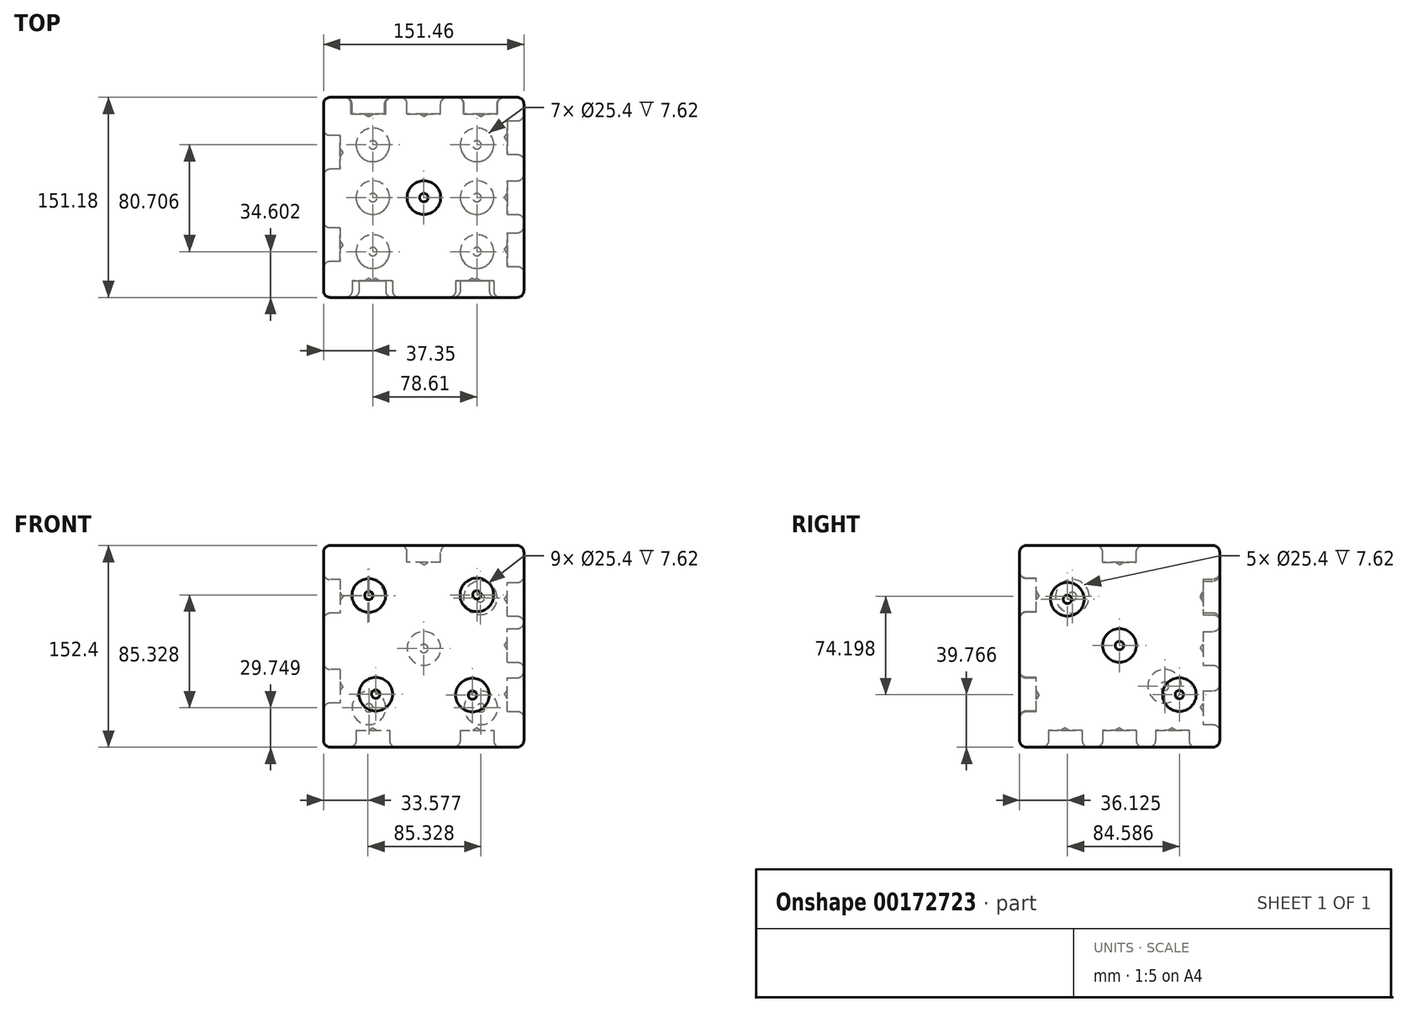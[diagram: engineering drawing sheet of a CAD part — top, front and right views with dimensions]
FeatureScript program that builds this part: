
annotation { "Feature Type Name" : "Feature", "Feature Type Description" : "" }
export const myFeature = defineFeature(function(context is Context, id is Id, definition is map)
    precondition{}
    {
        {
            var Q0;
            Q0=qCreatedBy(makeId("Top.planeOp"),FACE);
            var sketch = newSketch(context, id + "F0", { "sketchPlane" : qUnion([Q0])});
            skLineSegment(sketch, "E0.bottom", {"start": v(-75.87, -75.45) * mm, "end": v(75.59, -75.45) * mm});
            skLineSegment(sketch, "E0.top", {"start": v(-75.87, 75.73) * mm, "end": v(75.59, 75.73) * mm});
            skLineSegment(sketch, "E0.left", {"start": v(-75.87, -75.45) * mm, "end": v(-75.87, 75.73) * mm});
            skLineSegment(sketch, "E0.right", {"start": v(75.59, -75.45) * mm, "end": v(75.59, 75.73) * mm});
            skSolve(sketch);
        }
        {
            var Q0;
            Q0=makeQuery(id+"F0.imprint","IMPRINT",FACE,{"disambiguationData":[TD([[makeQuery(id+"F0.imprint","IMPRINT",EDGE,{"derivedFrom":sQuery(id+"F0.wireOp",EDGE,"E0.bottom")}),1.0]])]});
            extrude(context, id + "F1", {"entities" : qUnion([Q0]), "depth" : 127 * mm});
        }
        {
            var Q0;
            Q0=makeQuery(id+"F1.opExtrude","CAP_FACE",FACE,{"disambiguationData":[OSD([sQuery(id+"F0.wireOp",EDGE,"E0.bottom"),sQuery(id+"F0.wireOp",EDGE,"E0.top"),sQuery(id+"F0.wireOp",EDGE,"E0.left"),sQuery(id+"F0.wireOp",EDGE,"E0.right")])],"isStart":false});
            extrude(context, id + "F2", {"entities" : qUnion([Q0]), "operationType" : NewBodyOperationType.ADD, "depth" : 25.4 * mm});
        }
        {
            var Q0;
            Q0=makeQuery(id+"F2.opExtrude","CAP_FACE",FACE,{"disambiguationData":[OSD([sQuery(id+"F0.wireOp",EDGE,"E0.bottom"),sQuery(id+"F0.wireOp",EDGE,"E0.top"),sQuery(id+"F0.wireOp",EDGE,"E0.left"),sQuery(id+"F0.wireOp",EDGE,"E0.right")])],"isStart":false});
            var sketch = newSketch(context, id + "F3", { "sketchPlane" : qUnion([Q0])});
            skCircle(sketch, "E1", {"center": v(0, 0) * mm, "radius": 13.7 * mm});
            skSolve(sketch);
        }
        {
            var Q0;
            Q0=sQuery(id+"F3.wireOp",VERTEX,"E1.center");
            var Q1;
            Q1=makeQuery(id+"F1.opExtrude","SWEPT_BODY",BODY,{"disambiguationData":[OSD([sQuery(id+"F0.wireOp",EDGE,"E0.bottom"),sQuery(id+"F0.wireOp",EDGE,"E0.top"),sQuery(id+"F0.wireOp",EDGE,"E0.left"),sQuery(id+"F0.wireOp",EDGE,"E0.right")])]});
            hole(context, id + "F4", {"style" : HoleStyle.C_BORE, "endStyle" : HoleEndStyle.BLIND, "holeDiameter" : 6.35 * mm, "cBoreDiameter" : 25.4 * mm, "cBoreDepth" : 12.7 * mm, "holeDepth" : 12.7 * mm, "startFromSketch" : true, "locations" : qUnion([Q0]), "scope" : qUnion([Q1])});
        }
        {
            var Q0;
            Q0=makeQuery(id+"F4.hole-0.boolean.opBoolean","COPY",FACE,{"derivedFrom":makeQuery(id+"F4.hole-0.opRevolve","SWEPT_FACE",FACE,{"disambiguationData":[OSD([sQuery(id+"F4.hole-0.sketch.wireOp",EDGE,"cbore_start_line_2")])]})});
            var Q1;
            Q1=makeQuery(id+"F2.opExtrude","CAP_FACE",FACE,{"disambiguationData":[OSD([sQuery(id+"F0.wireOp",EDGE,"E0.bottom"),sQuery(id+"F0.wireOp",EDGE,"E0.top"),sQuery(id+"F0.wireOp",EDGE,"E0.left"),sQuery(id+"F0.wireOp",EDGE,"E0.right")])],"isStart":false});
            fillet(context, id + "F5", {"entities" : qUnion([Q0, Q1]), "radius" : 5.08 * mm, "tangentPropagation" : true, "allowEdgeOverflow" : false});
        }
        {
            var Q0;
            {var subQ0=sQuery(id+"F0.wireOp",EDGE,"E0.bottom");Q0=makeQuery(id+"F2.boolean.opBoolean","MERGE",FACE,{"derivedFrom":[makeQuery(id+"F1.opExtrude","SWEPT_FACE",FACE,{"disambiguationData":[OSD([subQ0])]}),makeQuery(id+"F2.opExtrude","SWEPT_FACE",FACE,{"disambiguationData":[OSD([subQ0])]})]});}
            var sketch = newSketch(context, id + "F6", { "sketchPlane" : qUnion([Q0])});
            skCircle(sketch, "E2", {"center": v(-36.36, 40.14) * mm, "radius": 16.76 * mm});
            skCircle(sketch, "E3", {"center": v(36.73, 39.4) * mm, "radius": 16.1 * mm});
            skCircle(sketch, "E4", {"center": v(40.07, 115.08) * mm, "radius": 15.97 * mm});
            skCircle(sketch, "E5", {"center": v(-41.55, 114.7) * mm, "radius": 15.44 * mm});
            skSolve(sketch);
        }
        {
            var Q0;
            Q0=sQuery(id+"F6.wireOp",VERTEX,"E4.center");
            var Q1;
            Q1=sQuery(id+"F6.wireOp",VERTEX,"E5.center");
            var Q2;
            Q2=sQuery(id+"F6.wireOp",VERTEX,"E2.center");
            var Q3;
            Q3=sQuery(id+"F6.wireOp",VERTEX,"E3.center");
            var Q4;
            Q4=makeQuery(id+"F1.opExtrude","SWEPT_BODY",BODY,{"disambiguationData":[OSD([sQuery(id+"F0.wireOp",EDGE,"E0.bottom"),sQuery(id+"F0.wireOp",EDGE,"E0.top"),sQuery(id+"F0.wireOp",EDGE,"E0.left"),sQuery(id+"F0.wireOp",EDGE,"E0.right")])]});
            hole(context, id + "F7", {"style" : HoleStyle.C_BORE, "endStyle" : HoleEndStyle.BLIND, "holeDiameter" : 6.35 * mm, "cBoreDiameter" : 25.4 * mm, "cBoreDepth" : 12.7 * mm, "holeDepth" : 12.7 * mm, "startFromSketch" : true, "locations" : qUnion([Q0, Q1, Q2, Q3]), "scope" : qUnion([Q4])});
        }
        {
            var Q0;
            {var subQ0=sQuery(id+"F0.wireOp",EDGE,"E0.bottom");Q0=makeQuery(id+"F2.boolean.opBoolean","MERGE",FACE,{"derivedFrom":[makeQuery(id+"F1.opExtrude","SWEPT_FACE",FACE,{"disambiguationData":[OSD([subQ0])]}),makeQuery(id+"F2.opExtrude","SWEPT_FACE",FACE,{"disambiguationData":[OSD([subQ0])]})]});}
            fillet(context, id + "F8", {"entities" : qUnion([Q0]), "radius" : 5.08 * mm, "tangentPropagation" : true, "allowEdgeOverflow" : false});
        }
        {
            var Q0;
            {var subQ0=sQuery(id+"F0.wireOp",EDGE,"E0.right");Q0=makeQuery(id+"F2.boolean.opBoolean","MERGE",FACE,{"derivedFrom":[makeQuery(id+"F1.opExtrude","SWEPT_FACE",FACE,{"disambiguationData":[OSD([subQ0])]}),makeQuery(id+"F2.opExtrude","SWEPT_FACE",FACE,{"disambiguationData":[OSD([subQ0])]})]});}
            var sketch = newSketch(context, id + "F9", { "sketchPlane" : qUnion([Q0])});
            skCircle(sketch, "E6", {"center": v(-39.32, 111.74) * mm, "radius": 16.7 * mm});
            skCircle(sketch, "E7", {"center": v(0, 76.86) * mm, "radius": 16.67 * mm});
            skCircle(sketch, "E8", {"center": v(45.26, 39.77) * mm, "radius": 17.37 * mm});
            skSolve(sketch);
        }
        {
            var Q0;
            Q0=sQuery(id+"F9.wireOp",VERTEX,"E7.center");
            var Q1;
            Q1=sQuery(id+"F9.wireOp",VERTEX,"E8.center");
            var Q2;
            Q2=sQuery(id+"F9.wireOp",VERTEX,"E6.center");
            var Q3;
            Q3=makeQuery(id+"F1.opExtrude","SWEPT_BODY",BODY,{"disambiguationData":[OSD([sQuery(id+"F0.wireOp",EDGE,"E0.bottom"),sQuery(id+"F0.wireOp",EDGE,"E0.top"),sQuery(id+"F0.wireOp",EDGE,"E0.left"),sQuery(id+"F0.wireOp",EDGE,"E0.right")])]});
            hole(context, id + "F10", {"style" : HoleStyle.C_BORE, "endStyle" : HoleEndStyle.BLIND, "holeDiameter" : 6.35 * mm, "cBoreDiameter" : 25.4 * mm, "cBoreDepth" : 12.7 * mm, "holeDepth" : 12.7 * mm, "startFromSketch" : true, "locations" : qUnion([Q0, Q1, Q2]), "scope" : qUnion([Q3])});
        }
        {
            var Q0;
            {var subQ0=sQuery(id+"F0.wireOp",EDGE,"E0.right");Q0=makeQuery(id+"F2.boolean.opBoolean","MERGE",FACE,{"derivedFrom":[makeQuery(id+"F1.opExtrude","SWEPT_FACE",FACE,{"disambiguationData":[OSD([subQ0])]}),makeQuery(id+"F2.opExtrude","SWEPT_FACE",FACE,{"disambiguationData":[OSD([subQ0])]})]});}
            fillet(context, id + "F11", {"entities" : qUnion([Q0]), "radius" : 5.08 * mm, "tangentPropagation" : true, "allowEdgeOverflow" : false});
        }
        {
            var Q0;
            {var subQ0=sQuery(id+"F0.wireOp",EDGE,"E0.left");Q0=makeQuery(id+"F2.boolean.opBoolean","MERGE",FACE,{"derivedFrom":[makeQuery(id+"F1.opExtrude","SWEPT_FACE",FACE,{"disambiguationData":[OSD([subQ0])]}),makeQuery(id+"F2.opExtrude","SWEPT_FACE",FACE,{"disambiguationData":[OSD([subQ0])]})]});}
            var sketch = newSketch(context, id + "F12", { "sketchPlane" : qUnion([Q0])});
            skCircle(sketch, "E9", {"center": v(-34.13, 46.07) * mm, "radius": 16.73 * mm});
            skCircle(sketch, "E10", {"center": v(35.61, 113.96) * mm, "radius": 16.53 * mm});
            skSolve(sketch);
        }
        {
            var Q0;
            Q0=sQuery(id+"F12.wireOp",VERTEX,"E9.center");
            var Q1;
            Q1=sQuery(id+"F12.wireOp",VERTEX,"E10.center");
            var Q2;
            Q2=makeQuery(id+"F1.opExtrude","SWEPT_BODY",BODY,{"disambiguationData":[OSD([sQuery(id+"F0.wireOp",EDGE,"E0.bottom"),sQuery(id+"F0.wireOp",EDGE,"E0.top"),sQuery(id+"F0.wireOp",EDGE,"E0.left"),sQuery(id+"F0.wireOp",EDGE,"E0.right")])]});
            hole(context, id + "F13", {"style" : HoleStyle.C_BORE, "endStyle" : HoleEndStyle.BLIND, "holeDiameter" : 6.35 * mm, "cBoreDiameter" : 25.4 * mm, "cBoreDepth" : 12.7 * mm, "holeDepth" : 12.7 * mm, "startFromSketch" : true, "locations" : qUnion([Q0, Q1]), "scope" : qUnion([Q2])});
        }
        {
            var Q0;
            {var subQ0=sQuery(id+"F0.wireOp",EDGE,"E0.left");Q0=makeQuery(id+"F2.boolean.opBoolean","MERGE",FACE,{"derivedFrom":[makeQuery(id+"F1.opExtrude","SWEPT_FACE",FACE,{"disambiguationData":[OSD([subQ0])]}),makeQuery(id+"F2.opExtrude","SWEPT_FACE",FACE,{"disambiguationData":[OSD([subQ0])]})]});}
            fillet(context, id + "F14", {"entities" : qUnion([Q0]), "radius" : 5.08 * mm, "tangentPropagation" : true, "allowEdgeOverflow" : false});
        }
        {
            var Q0;
            {var subQ0=sQuery(id+"F0.wireOp",EDGE,"E0.top");Q0=makeQuery(id+"F2.boolean.opBoolean","MERGE",FACE,{"derivedFrom":[makeQuery(id+"F1.opExtrude","SWEPT_FACE",FACE,{"disambiguationData":[OSD([subQ0])]}),makeQuery(id+"F2.opExtrude","SWEPT_FACE",FACE,{"disambiguationData":[OSD([subQ0])]})]});}
            var sketch = newSketch(context, id + "F15", { "sketchPlane" : qUnion([Q0])});
            skCircle(sketch, "E11", {"center": v(0, 74.64) * mm, "radius": 16.9 * mm});
            skCircle(sketch, "E12", {"center": v(-42.66, 112.85) * mm, "radius": 16.96 * mm});
            skCircle(sketch, "E13", {"center": v(42.3, 114.33) * mm, "radius": 16.36 * mm});
            skCircle(sketch, "E14", {"center": v(-43.03, 29.75) * mm, "radius": 16.7 * mm});
            skCircle(sketch, "E15", {"center": v(41.55, 29.75) * mm, "radius": 16.7 * mm});
            skSolve(sketch);
        }
        {
            var Q0;
            Q0=sQuery(id+"F15.wireOp",VERTEX,"E12.center");
            var Q1;
            Q1=sQuery(id+"F15.wireOp",VERTEX,"E13.center");
            var Q2;
            Q2=sQuery(id+"F15.wireOp",VERTEX,"E11.center");
            var Q3;
            Q3=sQuery(id+"F15.wireOp",VERTEX,"E15.center");
            var Q4;
            Q4=sQuery(id+"F15.wireOp",VERTEX,"E14.center");
            var Q5;
            Q5=makeQuery(id+"F1.opExtrude","SWEPT_BODY",BODY,{"disambiguationData":[OSD([sQuery(id+"F0.wireOp",EDGE,"E0.bottom"),sQuery(id+"F0.wireOp",EDGE,"E0.top"),sQuery(id+"F0.wireOp",EDGE,"E0.left"),sQuery(id+"F0.wireOp",EDGE,"E0.right")])]});
            hole(context, id + "F16", {"style" : HoleStyle.C_BORE, "endStyle" : HoleEndStyle.BLIND, "holeDiameter" : 6.35 * mm, "cBoreDiameter" : 25.4 * mm, "cBoreDepth" : 12.7 * mm, "holeDepth" : 12.7 * mm, "startFromSketch" : true, "locations" : qUnion([Q0, Q1, Q2, Q3, Q4]), "scope" : qUnion([Q5])});
        }
        {
            var Q0;
            {var subQ0=sQuery(id+"F0.wireOp",EDGE,"E0.top");Q0=makeQuery(id+"F2.boolean.opBoolean","MERGE",FACE,{"derivedFrom":[makeQuery(id+"F1.opExtrude","SWEPT_FACE",FACE,{"disambiguationData":[OSD([subQ0])]}),makeQuery(id+"F2.opExtrude","SWEPT_FACE",FACE,{"disambiguationData":[OSD([subQ0])]})]});}
            fillet(context, id + "F17", {"entities" : qUnion([Q0]), "radius" : 5.08 * mm, "tangentPropagation" : true, "allowEdgeOverflow" : false});
        }
        {
            var Q0;
            Q0=makeQuery(id+"F1.opExtrude","CAP_FACE",FACE,{"disambiguationData":[OSD([sQuery(id+"F0.wireOp",EDGE,"E0.bottom"),sQuery(id+"F0.wireOp",EDGE,"E0.top"),sQuery(id+"F0.wireOp",EDGE,"E0.left"),sQuery(id+"F0.wireOp",EDGE,"E0.right")])],"isStart":true});
            var sketch = newSketch(context, id + "F18", { "sketchPlane" : qUnion([Q0])});
            skCircle(sketch, "E16", {"center": v(-38.52, 40.85) * mm, "radius": 13.39 * mm});
            skCircle(sketch, "E17", {"center": v(-38.52, 0) * mm, "radius": 13.08 * mm});
            skCircle(sketch, "E18", {"center": v(-38.52, -39.86) * mm, "radius": 12.84 * mm});
            skCircle(sketch, "E19", {"center": v(40.09, 0) * mm, "radius": 13.72 * mm});
            skCircle(sketch, "E20", {"center": v(40.09, 40.85) * mm, "radius": 13.2 * mm});
            skCircle(sketch, "E21", {"center": v(40.09, -39.86) * mm, "radius": 12.84 * mm});
            skSolve(sketch);
        }
        {
            var Q0;
            Q0=sQuery(id+"F18.wireOp",VERTEX,"E20.center");
            var Q1;
            Q1=sQuery(id+"F18.wireOp",VERTEX,"E16.center");
            var Q2;
            Q2=sQuery(id+"F18.wireOp",VERTEX,"E19.center");
            var Q3;
            Q3=sQuery(id+"F18.wireOp",VERTEX,"E17.center");
            var Q4;
            Q4=sQuery(id+"F18.wireOp",VERTEX,"E18.center");
            var Q5;
            Q5=sQuery(id+"F18.wireOp",VERTEX,"E21.center");
            var Q6;
            Q6=makeQuery(id+"F1.opExtrude","SWEPT_BODY",BODY,{"disambiguationData":[OSD([sQuery(id+"F0.wireOp",EDGE,"E0.bottom"),sQuery(id+"F0.wireOp",EDGE,"E0.top"),sQuery(id+"F0.wireOp",EDGE,"E0.left"),sQuery(id+"F0.wireOp",EDGE,"E0.right")])]});
            hole(context, id + "F19", {"style" : HoleStyle.C_BORE, "endStyle" : HoleEndStyle.BLIND, "holeDiameter" : 6.35 * mm, "cBoreDiameter" : 25.4 * mm, "cBoreDepth" : 12.7 * mm, "holeDepth" : 12.7 * mm, "startFromSketch" : true, "locations" : qUnion([Q0, Q1, Q2, Q3, Q4, Q5]), "scope" : qUnion([Q6])});
        }
        {
            var Q0;
            Q0=makeQuery(id+"F1.opExtrude","CAP_FACE",FACE,{"disambiguationData":[OSD([sQuery(id+"F0.wireOp",EDGE,"E0.bottom"),sQuery(id+"F0.wireOp",EDGE,"E0.top"),sQuery(id+"F0.wireOp",EDGE,"E0.left"),sQuery(id+"F0.wireOp",EDGE,"E0.right")])],"isStart":true});
            fillet(context, id + "F20", {"entities" : qUnion([Q0]), "radius" : 5.08 * mm, "tangentPropagation" : true, "allowEdgeOverflow" : false});
        }
    });
